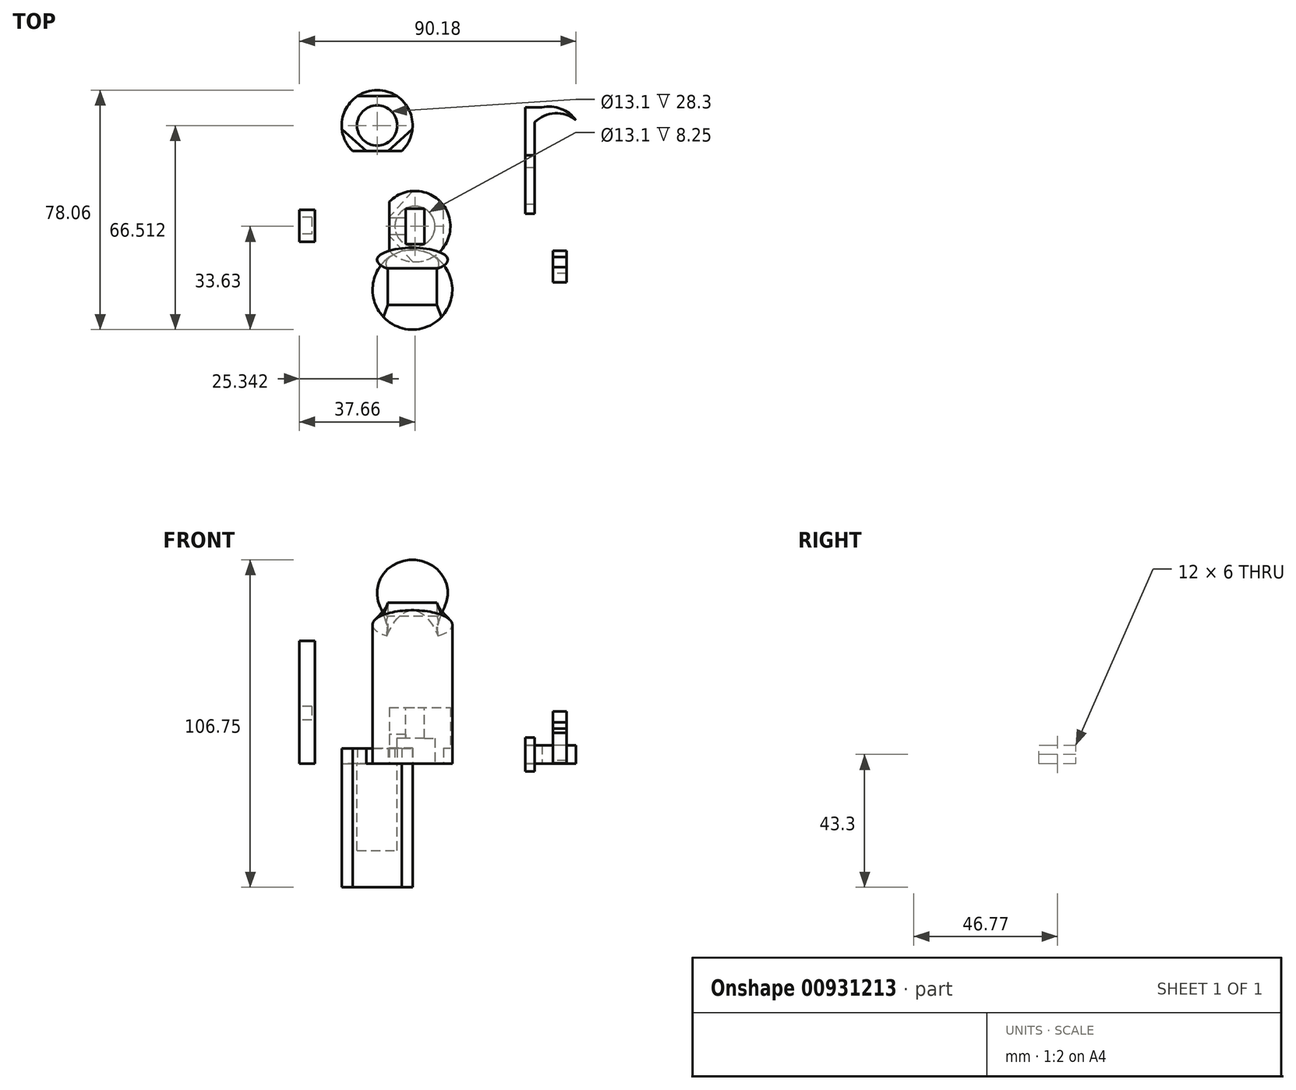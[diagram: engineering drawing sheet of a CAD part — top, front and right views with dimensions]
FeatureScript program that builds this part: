
annotation { "Feature Type Name" : "Feature", "Feature Type Description" : "" }
export const myFeature = defineFeature(function(context is Context, id is Id, definition is map)
    precondition{}
    {
        {
            var Q0;
            Q0=qCreatedBy(makeId("Top.planeOp"),FACE);
            var sketch = newSketch(context, id + "F0", { "sketchPlane" : qUnion([Q0])});
            skCircle(sketch, "E0", {"center": v(0, 0) * mm, "radius": 6.55 * mm});
            skCircle(sketch, "E1", {"center": v(0, 0) * mm, "radius": 11.55 * mm});
            skSolve(sketch);
        }
        {
            var Q0;
            Q0=makeQuery(id+"F0.imprint","IMPRINT",FACE,{"disambiguationData":[TD([[makeQuery(id+"F0.imprint","IMPRINT",EDGE,{"derivedFrom":sQuery(id+"F0.wireOp",EDGE,"E0")}),-1.0]])]});
            extrude(context, id + "F1", {"entities" : qUnion([Q0]), "depth" : (36.5 / 2) * mm, "offsetDistance" : 25 * mm});
        }
        {
            var Q0;
            Q0=makeQuery(id+"F1.opExtrude","CAP_FACE",FACE,{"disambiguationData":[OSD([sQuery(id+"F0.wireOp",EDGE,"E0"),sQuery(id+"F0.wireOp",EDGE,"E1")])],"isStart":false});
            var sketch = newSketch(context, id + "F2", { "sketchPlane" : qUnion([Q0])});
            skLineSegment(sketch, "E2", {"start": v(-3.05, 5.8) * mm, "end": v(-3.05, -5.8) * mm});
            skLineSegment(sketch, "E3", {"start": v(3.05, 5.8) * mm, "end": v(3.05, -5.8) * mm});
            skSolve(sketch);
        }
        {
            var Q0;
            {var subQ0=sQuery(id+"F2.wireOp",EDGE,"E3");Q0=makeQuery(id+"F2.imprint","IMPRINT",FACE,{"disambiguationData":[TD([[makeQuery(id+"F2.imprint","IMPRINT",EDGE,{"derivedFrom":subQ0}),1.0]])]});}
            var Q1;
            {var subQ0=sQuery(id+"F2.wireOp",EDGE,"E2");Q1=makeQuery(id+"F2.imprint","IMPRINT",FACE,{"disambiguationData":[TD([[makeQuery(id+"F2.imprint","IMPRINT",EDGE,{"derivedFrom":subQ0}),-1.0]])]});}
            extrude(context, id + "F3", {"entities" : qUnion([Q0, Q1]), "operationType" : NewBodyOperationType.ADD, "oppositeDirection" : true, "depth" : 10 * mm, "offsetDistance" : 25 * mm});
        }
        {
            var Q0;
            Q0=qCreatedBy(makeId("Top.planeOp"),FACE);
            var sketch = newSketch(context, id + "F4", { "sketchPlane" : qUnion([Q0])});
            skCircle(sketch, "E4", {"center": v(-12.32, 32.88) * mm, "radius": 6.55 * mm});
            skCircle(sketch, "E5", {"center": v(-12.32, 32.88) * mm, "radius": 11.55 * mm});
            skSolve(sketch);
        }
        {
            var Q0;
            Q0=makeQuery(id+"F4.imprint","IMPRINT",FACE,{"disambiguationData":[TD([[makeQuery(id+"F4.imprint","IMPRINT",EDGE,{"derivedFrom":sQuery(id+"F4.wireOp",EDGE,"E4")}),-1.0]])]});
            extrude(context, id + "F5", {"entities" : qUnion([Q0]), "oppositeDirection" : true, "depth" : (36.6 / 2 + 12) * mm, "offsetDistance" : 25 * mm});
        }
        {
            var Q0;
            Q0=makeQuery(id+"F5.opExtrude","CAP_FACE",FACE,{"disambiguationData":[OSD([sQuery(id+"F4.wireOp",EDGE,"E4"),sQuery(id+"F4.wireOp",EDGE,"E5")])],"isStart":false});
            var sketch = newSketch(context, id + "F6", { "sketchPlane" : qUnion([Q0])});
            skCircle(sketch, "E6", {"center": v(-12.32, -32.88) * mm, "radius": 6.55 * mm});
            skSolve(sketch);
        }
        {
            var Q0;
            Q0=makeQuery(id+"F6.imprint","IMPRINT",FACE,{"disambiguationData":[TD([[makeQuery(id+"F6.imprint","IMPRINT",EDGE,{"derivedFrom":sQuery(id+"F6.wireOp",EDGE,"E6")}),-1.0]])]});
            extrude(context, id + "F7", {"entities" : qUnion([Q0]), "operationType" : NewBodyOperationType.ADD, "oppositeDirection" : true, "depth" : 2 * mm, "offsetDistance" : 25 * mm});
        }
        {
            var Q0;
            Q0=makeQuery(id+"F7.boolean.opBoolean","MERGE",FACE,{"derivedFrom":[makeQuery(id+"F5.opExtrude","CAP_FACE",FACE,{"disambiguationData":[OSD([sQuery(id+"F4.wireOp",EDGE,"E4"),sQuery(id+"F4.wireOp",EDGE,"E5")])],"isStart":false}),makeQuery(id+"F7.opExtrude","CAP_FACE",FACE,{"disambiguationData":[OSD([sQuery(id+"F6.wireOp",EDGE,"E6")])],"isStart":true})]});
            var sketch = newSketch(context, id + "F8", { "sketchPlane" : qUnion([Q0])});
            skLineSegment(sketch, "E7", {"start": v(-20.32, -24.55) * mm, "end": v(-4.32, -24.55) * mm});
            skSolve(sketch);
        }
        {
            var Q0;
            {var subQ0=sQuery(id+"F8.wireOp",EDGE,"E7");Q0=makeQuery(id+"F8.imprint","IMPRINT",FACE,{"disambiguationData":[TD([[makeQuery(id+"F8.imprint","IMPRINT",EDGE,{"derivedFrom":subQ0}),1.0]])]});}
            extrude(context, id + "F9", {"entities" : qUnion([Q0]), "operationType" : NewBodyOperationType.REMOVE, "oppositeDirection" : true, "depth" : 40 * mm, "offsetDistance" : 25 * mm});
        }
        {
            var Q0;
            Q0=makeQuery(id+"F1.opExtrude","CAP_FACE",FACE,{"disambiguationData":[OSD([sQuery(id+"F0.wireOp",EDGE,"E0"),sQuery(id+"F0.wireOp",EDGE,"E1")])],"isStart":true});
            var sketch = newSketch(context, id + "F10", { "sketchPlane" : qUnion([Q0])});
            skLineSegment(sketch, "E8", {"start": v(-8.33, -8) * mm, "end": v(-8.33, 8) * mm});
            skSolve(sketch);
        }
        {
            var Q0;
            {var subQ0=sQuery(id+"F10.wireOp",EDGE,"E8");Q0=makeQuery(id+"F10.imprint","IMPRINT",FACE,{"disambiguationData":[TD([[makeQuery(id+"F10.imprint","IMPRINT",EDGE,{"derivedFrom":subQ0}),1.0]])]});}
            extrude(context, id + "F11", {"entities" : qUnion([Q0]), "operationType" : NewBodyOperationType.REMOVE, "oppositeDirection" : true, "depth" : 25 * mm, "offsetDistance" : 25 * mm});
        }
        {
            var Q0;
            Q0=makeQuery(id+"F11.boolean.opBoolean","COPY",FACE,{"derivedFrom":makeQuery(id+"F11.opExtrude","SWEPT_FACE",FACE,{"disambiguationData":[OSD([sQuery(id+"F10.wireOp",EDGE,"E8")])]})});
            var sketch = newSketch(context, id + "F12", { "sketchPlane" : qUnion([Q0])});
            skLineSegment(sketch, "E9.bottom", {"start": v(-2.75, 9.5) * mm, "end": v(2.75, 9.5) * mm});
            skLineSegment(sketch, "E9.top", {"start": v(-2.75, 5) * mm, "end": v(2.75, 5) * mm});
            skLineSegment(sketch, "E9.left", {"start": v(-2.75, 9.5) * mm, "end": v(-2.75, 5) * mm});
            skLineSegment(sketch, "E9.right", {"start": v(2.75, 9.5) * mm, "end": v(2.75, 5) * mm});
            skLineSegment(sketch, "E10", {"start": v(-2.75, 7.25) * mm, "end": v(-8, 7.25) * mm});
            skLineSegment(sketch, "E11", {"start": v(2.75, 7.25) * mm, "end": v(8, 7.25) * mm});
            skSolve(sketch);
        }
        {
            var Q0;
            Q0=qSketchRegion(id+"F12",true);
            extrude(context, id + "F13", {"entities" : qUnion([Q0]), "operationType" : NewBodyOperationType.REMOVE, "oppositeDirection" : true, "depth" : 10 * mm, "offsetDistance" : 25 * mm});
        }
        {
            var Q0;
            Q0=qCreatedBy(makeId("Top.planeOp"),FACE);
            var sketch = newSketch(context, id + "F14", { "sketchPlane" : qUnion([Q0])});
            skLineSegment(sketch, "E12.bottom", {"start": v(49.4, -13.29) * mm, "end": v(45, -13.29) * mm});
            skLineSegment(sketch, "E12.top", {"start": v(49.4, -9.99) * mm, "end": v(45, -9.99) * mm});
            skLineSegment(sketch, "E12.left", {"start": v(49.4, -13.29) * mm, "end": v(49.4, -9.99) * mm});
            skLineSegment(sketch, "E12.right", {"start": v(45, -13.29) * mm, "end": v(45, -9.99) * mm});
            skSolve(sketch);
        }
        {
            var Q0;
            Q0=qSketchRegion(id+"F14",true);
            extrude(context, id + "F15", {"entities" : qUnion([Q0]), "depth" : 30 * mm, "offsetDistance" : 25 * mm});
        }
        {
            var Q0;
            {var subQ0=sQuery(id+"F0.wireOp",EDGE,"E0");Q0=makeQuery(id+"F3.boolean.opBoolean","MERGE",FACE,{"derivedFrom":[makeQuery(id+"F1.opExtrude","CAP_FACE",FACE,{"disambiguationData":[OSD([subQ0,sQuery(id+"F0.wireOp",EDGE,"E1")])],"isStart":false}),makeQuery(id+"F3.opExtrude","CAP_FACE",FACE,{"disambiguationData":[OSD([subQ0,sQuery(id+"F2.wireOp",EDGE,"E2")])],"isStart":true}),makeQuery(id+"F3.opExtrude","CAP_FACE",FACE,{"disambiguationData":[OSD([subQ0,sQuery(id+"F2.wireOp",EDGE,"E3")])],"isStart":true})]});}
            var sketch = newSketch(context, id + "F16", { "sketchPlane" : qUnion([Q0])});
            skLineSegment(sketch, "E13", {"start": v(-3.05, 5.8) * mm, "end": v(3.05, 5.8) * mm});
            skLineSegment(sketch, "E14", {"start": v(3.05, -5.8) * mm, "end": v(-3.05, -5.8) * mm});
            skSolve(sketch);
        }
        {
            var Q0;
            Q0=makeQuery(id+"F16.imprint","IMPRINT",FACE,{"disambiguationData":[TD([[makeQuery(id+"F16.imprint","IMPRINT",EDGE,{"derivedFrom":sQuery(id+"F16.wireOp",EDGE,"E13")}),1.0]])]});
            var Q1;
            Q1=makeQuery(id+"F16.imprint","IMPRINT",FACE,{"disambiguationData":[TD([[makeQuery(id+"F16.imprint","IMPRINT",EDGE,{"derivedFrom":sQuery(id+"F16.wireOp",EDGE,"E14")}),1.0]])]});
            extrude(context, id + "F17", {"entities" : qUnion([Q0, Q1]), "operationType" : NewBodyOperationType.ADD, "oppositeDirection" : true, "depth" : 10 * mm, "offsetDistance" : 25 * mm});
        }
        {
            var Q0;
            Q0=qCreatedBy(makeId("Top.planeOp"),FACE);
            var sketch = newSketch(context, id + "F18", { "sketchPlane" : qUnion([Q0])});
            skLineSegment(sketch, "E15.bottom", {"start": v(-37.66, 5.43) * mm, "end": v(-32.66, 5.43) * mm});
            skLineSegment(sketch, "E15.top", {"start": v(-37.66, -4.97) * mm, "end": v(-32.66, -4.97) * mm});
            skLineSegment(sketch, "E15.left", {"start": v(-37.66, 5.43) * mm, "end": v(-37.66, -4.97) * mm});
            skLineSegment(sketch, "E15.right", {"start": v(-32.66, 5.43) * mm, "end": v(-32.66, -4.97) * mm});
            skSolve(sketch);
        }
        {
            var Q0;
            Q0=qSketchRegion(id+"F18",true);
            extrude(context, id + "F19", {"entities" : qUnion([Q0]), "depth" : 40 * mm, "offsetDistance" : 25 * mm});
        }
        {
            var Q0;
            Q0=makeQuery(id+"F19.opExtrude","SWEPT_FACE",FACE,{"disambiguationData":[OSD([sQuery(id+"F18.wireOp",EDGE,"E15.left")])]});
            var sketch = newSketch(context, id + "F20", { "sketchPlane" : qUnion([Q0])});
            skLineSegment(sketch, "E16.bottom", {"start": v(-2.98, 18.7) * mm, "end": v(2.52, 18.7) * mm});
            skLineSegment(sketch, "E16.top", {"start": v(-2.98, 14.2) * mm, "end": v(2.52, 14.2) * mm});
            skLineSegment(sketch, "E16.left", {"start": v(-2.98, 18.7) * mm, "end": v(-2.98, 14.2) * mm});
            skLineSegment(sketch, "E16.right", {"start": v(2.52, 18.7) * mm, "end": v(2.52, 14.2) * mm});
            skLineSegment(sketch, "E17", {"start": v(-2.98, 16.45) * mm, "end": v(-5.43, 16.45) * mm});
            skLineSegment(sketch, "E18", {"start": v(2.52, 16.45) * mm, "end": v(4.97, 16.45) * mm});
            skSolve(sketch);
        }
        {
            var Q0;
            Q0=qSketchRegion(id+"F20",true);
            extrude(context, id + "F21", {"entities" : qUnion([Q0]), "operationType" : NewBodyOperationType.REMOVE, "oppositeDirection" : true, "depth" : 4 * mm, "offsetDistance" : 25 * mm});
        }
        {
            var Q0;
            Q0=makeQuery(id+"F5.opExtrude","CAP_FACE",FACE,{"disambiguationData":[OSD([sQuery(id+"F4.wireOp",EDGE,"E4"),sQuery(id+"F4.wireOp",EDGE,"E5")])],"isStart":true});
            var sketch = newSketch(context, id + "F22", { "sketchPlane" : qUnion([Q0])});
            skLineSegment(sketch, "E19", {"start": v(-23.81, 31.73) * mm, "end": v(-15.83, 24.55) * mm});
            skLineSegment(sketch, "E20", {"start": v(-20.32, 24.55) * mm, "end": v(-18.31, 26.78) * mm});
            skLineSegment(sketch, "E21", {"start": v(-8.8, 24.55) * mm, "end": v(-0.83, 31.73) * mm});
            skLineSegment(sketch, "E22", {"start": v(-4.32, 24.55) * mm, "end": v(-6.33, 26.78) * mm});
            skLineSegment(sketch, "E23", {"start": v(-18.81, 42.43) * mm, "end": v(-5.82, 42.43) * mm});
            skLineSegment(sketch, "E24", {"start": v(-12.32, 44.43) * mm, "end": v(-12.32, 42.43) * mm});
            skSolve(sketch);
        }
        {
            var Q0;
            {var subQ3=sQuery(id+"F22.wireOp",EDGE,"E24");Q0=makeQuery(id+"F22.imprint","IMPRINT",FACE,{"disambiguationData":[TD([[makeQuery(id+"F22.imprint","IMPRINT",EDGE,{"derivedFrom":subQ3}),-1.0]])]});}
            var Q1;
            {var subQ3=sQuery(id+"F22.wireOp",EDGE,"E24");Q1=makeQuery(id+"F22.imprint","IMPRINT",FACE,{"disambiguationData":[TD([[makeQuery(id+"F22.imprint","IMPRINT",EDGE,{"derivedFrom":subQ3}),1.0]])]});}
            var Q2;
            {var subQ4=sQuery(id+"F22.wireOp",EDGE,"E22");Q2=makeQuery(id+"F22.imprint","IMPRINT",FACE,{"disambiguationData":[TD([[makeQuery(id+"F22.imprint","IMPRINT",EDGE,{"derivedFrom":subQ4}),-1.0]])]});}
            var Q3;
            {var subQ4=sQuery(id+"F22.wireOp",EDGE,"E22");Q3=makeQuery(id+"F22.imprint","IMPRINT",FACE,{"disambiguationData":[TD([[makeQuery(id+"F22.imprint","IMPRINT",EDGE,{"derivedFrom":subQ4}),1.0]])]});}
            var Q4;
            {var subQ4=sQuery(id+"F22.wireOp",EDGE,"E20");Q4=makeQuery(id+"F22.imprint","IMPRINT",FACE,{"disambiguationData":[TD([[makeQuery(id+"F22.imprint","IMPRINT",EDGE,{"derivedFrom":subQ4}),-1.0]])]});}
            var Q5;
            {var subQ4=sQuery(id+"F22.wireOp",EDGE,"E20");Q5=makeQuery(id+"F22.imprint","IMPRINT",FACE,{"disambiguationData":[TD([[makeQuery(id+"F22.imprint","IMPRINT",EDGE,{"derivedFrom":subQ4}),1.0]])]});}
            extrude(context, id + "F23", {"entities" : qUnion([Q0, Q1, Q2, Q3, Q4, Q5]), "operationType" : NewBodyOperationType.ADD, "depth" : 5 * mm, "offsetDistance" : 25 * mm});
        }
        {
            var Q0;
            Q0=makeQuery(id+"F1.opExtrude","CAP_FACE",FACE,{"disambiguationData":[OSD([sQuery(id+"F0.wireOp",EDGE,"E0"),sQuery(id+"F0.wireOp",EDGE,"E1")])],"isStart":true});
            var sketch = newSketch(context, id + "F24", { "sketchPlane" : qUnion([Q0])});
            skLineSegment(sketch, "E25", {"start": v(-0.71, 11.53) * mm, "end": v(-8.33, 3.07) * mm});
            skLineSegment(sketch, "E26", {"start": v(-0.71, -11.53) * mm, "end": v(-8.33, -3.07) * mm});
            skLineSegment(sketch, "E27", {"start": v(9.25, 6.92) * mm, "end": v(9.25, -6.92) * mm});
            skLineSegment(sketch, "E28", {"start": v(11.55, 0) * mm, "end": v(9.25, 0) * mm});
            skLineSegment(sketch, "E29", {"start": v(-8.33, -8) * mm, "end": v(-5.88, -5.8) * mm});
            skLineSegment(sketch, "E30", {"start": v(-8.33, 8) * mm, "end": v(-5.88, 5.8) * mm});
            skSolve(sketch);
        }
        {
            var Q0;
            {var subQ4=sQuery(id+"F24.wireOp",EDGE,"E29");Q0=makeQuery(id+"F24.imprint","IMPRINT",FACE,{"disambiguationData":[TD([[makeQuery(id+"F24.imprint","IMPRINT",EDGE,{"derivedFrom":subQ4}),1.0]])]});}
            var Q1;
            {var subQ5=sQuery(id+"F24.wireOp",EDGE,"E29");Q1=makeQuery(id+"F24.imprint","IMPRINT",FACE,{"disambiguationData":[TD([[makeQuery(id+"F24.imprint","IMPRINT",EDGE,{"derivedFrom":subQ5}),-1.0]])]});}
            var Q2;
            {var subQ5=sQuery(id+"F24.wireOp",EDGE,"E30");Q2=makeQuery(id+"F24.imprint","IMPRINT",FACE,{"disambiguationData":[TD([[makeQuery(id+"F24.imprint","IMPRINT",EDGE,{"derivedFrom":subQ5}),1.0]])]});}
            var Q3;
            {var subQ4=sQuery(id+"F24.wireOp",EDGE,"E30");Q3=makeQuery(id+"F24.imprint","IMPRINT",FACE,{"disambiguationData":[TD([[makeQuery(id+"F24.imprint","IMPRINT",EDGE,{"derivedFrom":subQ4}),-1.0]])]});}
            var Q4;
            {var subQ3=sQuery(id+"F24.wireOp",EDGE,"E28");Q4=makeQuery(id+"F24.imprint","IMPRINT",FACE,{"disambiguationData":[TD([[makeQuery(id+"F24.imprint","IMPRINT",EDGE,{"derivedFrom":subQ3}),1.0]])]});}
            var Q5;
            {var subQ3=sQuery(id+"F24.wireOp",EDGE,"E28");Q5=makeQuery(id+"F24.imprint","IMPRINT",FACE,{"disambiguationData":[TD([[makeQuery(id+"F24.imprint","IMPRINT",EDGE,{"derivedFrom":subQ3}),-1.0]])]});}
            extrude(context, id + "F25", {"entities" : qUnion([Q0, Q1, Q2, Q3, Q4, Q5]), "operationType" : NewBodyOperationType.REMOVE, "oppositeDirection" : true, "depth" : 5.1 * mm, "offsetDistance" : 25 * mm});
        }
        {
            var Q0;
            Q0=makeQuery(id+"F15.opExtrude","CAP_EDGE",EDGE,{"disambiguationData":[OSD([sQuery(id+"F14.wireOp",EDGE,"E12.top")])],"isStart":true});
            chamfer(context, id + "F26", {"entities" : qUnion([Q0]), "chamferType" : ChamferType.TWO_OFFSETS, "width1" : 3.7 * mm, "oppositeDirection" : false, "width2" : 1 * mm});
        }
        {
            var Q0;
            Q0=makeQuery(id+"F15.opExtrude","CAP_FACE",FACE,{"disambiguationData":[OSD([sQuery(id+"F14.wireOp",EDGE,"E12.bottom"),sQuery(id+"F14.wireOp",EDGE,"E12.top"),sQuery(id+"F14.wireOp",EDGE,"E12.left"),sQuery(id+"F14.wireOp",EDGE,"E12.right")])],"isStart":false});
            var sketch = newSketch(context, id + "F27", { "sketchPlane" : qUnion([Q0])});
            skLineSegment(sketch, "E31.bottom", {"start": v(39.7, -13.29) * mm, "end": v(54.7, -13.29) * mm});
            skLineSegment(sketch, "E31.top", {"start": v(39.7, -8.29) * mm, "end": v(54.7, -8.29) * mm});
            skLineSegment(sketch, "E31.left", {"start": v(39.7, -13.29) * mm, "end": v(39.7, -8.29) * mm});
            skLineSegment(sketch, "E31.right", {"start": v(54.7, -13.29) * mm, "end": v(54.7, -8.29) * mm});
            skLineSegment(sketch, "E32", {"start": v(39.7, -9.99) * mm, "end": v(45, -9.99) * mm});
            skLineSegment(sketch, "E33", {"start": v(49.4, -9.99) * mm, "end": v(54.7, -9.99) * mm});
            skSolve(sketch);
        }
        {
            var Q0;
            {var subQ4=sQuery(id+"F27.wireOp",EDGE,"E32");Q0=makeQuery(id+"F27.imprint","IMPRINT",FACE,{"disambiguationData":[TD([[makeQuery(id+"F27.imprint","IMPRINT",EDGE,{"derivedFrom":subQ4}),-1.0]])]});}
            cPlane(context, id + "F28", {"entities" : qUnion([Q0]), "cplaneType" : CPlaneType.OFFSET, "offset" : 20 * mm, "oppositeDirection" : true, "width" : 150 * mm, "height" : 150 * mm});
        }
        {
            var Q0;
            Q0=qCreatedBy(id+"F28.planeOp",FACE);
            var sketch = newSketch(context, id + "F29", { "sketchPlane" : qUnion([Q0])});
            skLineSegment(sketch, "E34.0.0", {"start": v(45, -13.29) * mm, "end": v(45, -10.99) * mm});
            skLineSegment(sketch, "E34.0.1", {"start": v(45, -10.99) * mm, "end": v(49.4, -10.99) * mm});
            skLineSegment(sketch, "E34.0.2", {"start": v(49.4, -10.99) * mm, "end": v(49.4, -13.29) * mm});
            skLineSegment(sketch, "E34.0.3", {"start": v(49.4, -13.29) * mm, "end": v(45, -13.29) * mm});
            skLineSegment(sketch, "E35.bottom", {"start": v(42.2, -13.29) * mm, "end": v(52.2, -13.29) * mm});
            skLineSegment(sketch, "E35.top", {"start": v(42.2, -10.09) * mm, "end": v(52.2, -10.09) * mm});
            skLineSegment(sketch, "E35.left", {"start": v(42.2, -13.29) * mm, "end": v(42.2, -10.09) * mm});
            skLineSegment(sketch, "E35.right", {"start": v(52.2, -13.29) * mm, "end": v(52.2, -10.09) * mm});
            skLineSegment(sketch, "E36", {"start": v(45, -10.99) * mm, "end": v(42.2, -10.99) * mm});
            skLineSegment(sketch, "E37", {"start": v(49.4, -10.99) * mm, "end": v(52.2, -10.99) * mm});
            skSolve(sketch);
        }
        {
            var Q0;
            Q0=qCreatedBy(makeId("Top.planeOp"),FACE);
            var sketch = newSketch(context, id + "F30", { "sketchPlane" : qUnion([Q0])});
            skCircle(sketch, "E38", {"center": v(-0.83, -20.63) * mm, "radius": 13 * mm});
            skSolve(sketch);
        }
        {
            var Q0;
            Q0=makeQuery(id+"F30.imprint","IMPRINT",FACE,{"disambiguationData":[TD([[makeQuery(id+"F30.imprint","IMPRINT",EDGE,{"derivedFrom":sQuery(id+"F30.wireOp",EDGE,"E38")}),1.0]])]});
            extrude(context, id + "F31", {"entities" : qUnion([Q0]), "depth" : 50 * mm, "offsetDistance" : 25 * mm});
        }
        {
            var Q0;
            Q0=makeQuery(id+"F31.opExtrude","CAP_FACE",FACE,{"disambiguationData":[OSD([sQuery(id+"F30.wireOp",EDGE,"E38")])],"isStart":false});
            var sketch = newSketch(context, id + "F32", { "sketchPlane" : qUnion([Q0])});
            skLineSegment(sketch, "E39.bottom", {"start": v(-5.1, -22.85) * mm, "end": v(-0.43, -22.85) * mm});
            skLineSegment(sketch, "E39.top", {"start": v(-5.1, -18.54) * mm, "end": v(-0.43, -18.54) * mm});
            skLineSegment(sketch, "E39.left", {"start": v(-5.1, -22.85) * mm, "end": v(-5.1, -18.54) * mm});
            skLineSegment(sketch, "E39.right", {"start": v(-0.43, -22.85) * mm, "end": v(-0.43, -18.54) * mm});
            skSolve(sketch);
        }
        {
            var Q0;
            Q0 = qSketchRegion(id + "F32", true);
            extrude(context, id + "F33", {"entities" : qUnion([Q0]), "operationType" : NewBodyOperationType.REMOVE, "oppositeDirection" : true, "depth" : .1 * mm, "offsetDistance" : 25 * mm});
        }
        {
            var Q0;
            Q0=makeQuery(id+"F33.boolean.opBoolean","COPY",FACE,{"derivedFrom":makeQuery(id+"F33.opExtrude","SWEPT_FACE",FACE,{"disambiguationData":[OSD([sQuery(id+"F32.wireOp",EDGE,"E39.left")])]})});
            cPlane(context, id + "F34", {"entities" : qUnion([Q0]), "cplaneType" : CPlaneType.OFFSET, "offset" : 3 * mm, "width" : 150 * mm, "height" : 150 * mm});
        }
        {
            var Q0;
            Q0=qCreatedBy(id+"F34.planeOp",FACE);
            var sketch = newSketch(context, id + "F35", { "sketchPlane" : qUnion([Q0])});
            skLineSegment(sketch, "E40.0", {"start": v(-33.63, 50) * mm, "end": v(-7.63, 50) * mm});
            skLineSegment(sketch, "E41", {"start": v(-33.63, 0) * mm, "end": v(-33.63, 50) * mm});
            skLineSegment(sketch, "E42", {"start": v(-7.63, 50) * mm, "end": v(-7.63, 0) * mm});
            skLineSegment(sketch, "E43", {"start": v(-33.63, 50) * mm, "end": v(-10.67, 41.64) * mm});
            skLineSegment(sketch, "E44", {"start": v(-10.67, 41.64) * mm, "end": v(-7.63, 50) * mm});
            skSolve(sketch);
        }
        {
            var Q0;
            Q0 = qSketchRegion(id + "F35", true);
            extrude(context, id + "F36", {"entities" : qUnion([Q0]), "operationType" : NewBodyOperationType.REMOVE, "oppositeDirection" : true, "depth" : 30 * mm, "offsetDistance" : 25 * mm, "symmetric" : true});
        }
        {
            var Q0;
            Q0=makeQuery(id+"F36.boolean.opBoolean","COPY",FACE,{"derivedFrom":makeQuery(id+"F36.opExtrude","SWEPT_FACE",FACE,{"disambiguationData":[OSD([sQuery(id+"F35.wireOp",EDGE,"E44")])]})});
            cPlane(context, id + "F37", {"entities" : qUnion([Q0]), "cplaneType" : CPlaneType.OFFSET, "offset" : 5 * mm, "width" : 150 * mm, "height" : 150 * mm});
        }
        {
            var Q0;
            Q0=qCreatedBy(id+"F34.planeOp",FACE);
            var sketch = newSketch(context, id + "F38", { "sketchPlane" : qUnion([Q0])});
            skPoint(sketch, "E45.0", {"position": v(-10.67, 41.64) * mm});
            skLineSegment(sketch, "E46", {"start": v(-10.67, 41.64) * mm, "end": v(-10.67, 46.64) * mm});
            skSolve(sketch);
        }
        {
            var Q0;
            Q0=qCreatedBy(id+"F37.planeOp",FACE);
            var sketch = newSketch(context, id + "F39", { "sketchPlane" : qUnion([Q0])});
            skLineSegment(sketch, "E47", {"start": v(7.17, 40.18) * mm, "end": v(-8.83, 40.18) * mm});
            skArc(sketch, "E48", {"start": v(7.17, 40.18) * mm, "mid": v(-0.83, 60.06) * mm, "end": v(-8.83, 40.18) * mm});
            skLineSegment(sketch, "E49", {"start": v(12.17, 11.57) * mm, "end": v(12.17, -14.59) * mm});
            skLineSegment(sketch, "E50", {"start": v(-13.83, -14.59) * mm, "end": v(-13.83, 11.57) * mm});
            skPoint(sketch, "E51.0.start.orphan", {"position": v(7.53, 35.48) * mm});
            skPoint(sketch, "E52.trimOffspring.end.orphan", {"position": v(-9.18, 35.48) * mm});
            skSolve(sketch);
        }
        {
            var Q1;
            Q1=makeQuery(id+"F36.boolean.opBoolean","COPY",FACE,{"derivedFrom":makeQuery(id+"F36.opExtrude","SWEPT_FACE",FACE,{"disambiguationData":[OSD([sQuery(id+"F35.wireOp",EDGE,"E44")])]})});
            var Q2;
            Q2=makeQuery(id+"F39.imprint","IMPRINT",FACE,{"disambiguationData":[TD([[makeQuery(id+"F39.imprint","IMPRINT",EDGE,{"derivedFrom":sQuery(id+"F39.wireOp",EDGE,"E47")}),-1.0]])]});
            loft(context, id + "F40", {"operationType" : NewBodyOperationType.ADD, "sheetProfilesArray" : [{ "sheetProfileEntities" : qUnion([Q1]) }, { "sheetProfileEntities" : qUnion([Q2]) }]});
        }
        {
            var Q0;
            Q0=makeQuery(id+"F36.boolean.opBoolean","COPY",FACE,{"derivedFrom":makeQuery(id+"F36.opExtrude","SWEPT_FACE",FACE,{"disambiguationData":[OSD([sQuery(id+"F35.wireOp",EDGE,"E43")])]})});
            cPlane(context, id + "F41", {"entities" : qUnion([Q0]), "cplaneType" : CPlaneType.OFFSET, "offset" : 5 * mm, "width" : 150 * mm, "height" : 150 * mm});
        }
        {
            var Q0;
            Q0=qCreatedBy(id+"F41.planeOp",FACE);
            var sketch = newSketch(context, id + "F42", { "sketchPlane" : qUnion([Q0])});
            skLineSegment(sketch, "E53.bottom", {"start": v(-8.83, -41.98) * mm, "end": v(7.17, -41.98) * mm});
            skLineSegment(sketch, "E53.top", {"start": v(-8.83, -25.98) * mm, "end": v(7.17, -25.98) * mm});
            skLineSegment(sketch, "E53.left", {"start": v(-8.83, -41.98) * mm, "end": v(-8.83, -25.98) * mm});
            skLineSegment(sketch, "E53.right", {"start": v(7.17, -41.98) * mm, "end": v(7.17, -25.98) * mm});
            skLineSegment(sketch, "E54", {"start": v(-13.83, -40.75) * mm, "end": v(-13.83, -14.59) * mm});
            skLineSegment(sketch, "E55", {"start": v(12.17, -14.59) * mm, "end": v(12.17, -40.75) * mm});
            skSolve(sketch);
        }
        {
            var Q1;
            Q1=makeQuery(id+"F36.boolean.opBoolean","COPY",FACE,{"derivedFrom":makeQuery(id+"F36.opExtrude","SWEPT_FACE",FACE,{"disambiguationData":[OSD([sQuery(id+"F35.wireOp",EDGE,"E43")])]})});
            var Q2;
            Q2=makeQuery(id+"F42.imprint","IMPRINT",FACE,{"disambiguationData":[TD([[makeQuery(id+"F42.imprint","IMPRINT",EDGE,{"derivedFrom":sQuery(id+"F42.wireOp",EDGE,"E53.bottom")}),1.0]])]});
            loft(context, id + "F43", {"operationType" : NewBodyOperationType.ADD, "sheetProfilesArray" : [{ "sheetProfileEntities" : qUnion([Q1]) }, { "sheetProfileEntities" : qUnion([Q2]) }]});
        }
        {
            var Q0;
            Q0=makeQuery(id+"F15.opExtrude","SWEPT_FACE",FACE,{"disambiguationData":[OSD([sQuery(id+"F14.wireOp",EDGE,"E12.right")])]});
            var sketch = newSketch(context, id + "F44", { "sketchPlane" : qUnion([Q0])});
            skLineSegment(sketch, "E56.0", {"start": v(10.99, 10) * mm, "end": v(13.29, 10) * mm});
            skLineSegment(sketch, "E57", {"start": v(13.29, 10) * mm, "end": v(18.29, 13.5) * mm});
            skLineSegment(sketch, "E58", {"start": v(18.29, 13.5) * mm, "end": v(13.29, 13.5) * mm});
            skSolve(sketch);
        }
        {
            var Q0;
            {var subQ0=sQuery(id+"F44.wireOp",EDGE,"E57");Q0=makeQuery(id+"F44.imprint","IMPRINT",FACE,{"disambiguationData":[TD([[makeQuery(id+"F44.imprint","IMPRINT",EDGE,{"derivedFrom":subQ0}),1.0]])]});}
            var Q1;
            Q1=makeQuery(id+"F15.opExtrude","SWEPT_FACE",FACE,{"disambiguationData":[OSD([sQuery(id+"F14.wireOp",EDGE,"E12.left")])]});
            extrude(context, id + "F45", {"entities" : qUnion([Q0]), "operationType" : NewBodyOperationType.ADD, "endBound" : BoundingType.UP_TO_SURFACE, "oppositeDirection" : true, "depth" : 25 * mm, "endBoundEntityFace" : qUnion([Q1]), "offsetDistance" : 25 * mm});
        }
        {
            var Q0;
            {var subQ0=sQuery(id+"F14.wireOp",EDGE,"E12.right");Q0=makeQuery(id+"F45.boolean.opBoolean","MERGE",FACE,{"derivedFrom":[makeQuery(id+"F15.opExtrude","SWEPT_FACE",FACE,{"disambiguationData":[OSD([subQ0])]}),makeQuery(id+"F45.opExtrude","CAP_FACE",FACE,{"disambiguationData":[OSD([sQuery(id+"F14.wireOp",EDGE,"E12.bottom"),subQ0,sQuery(id+"F44.wireOp",EDGE,"E57"),sQuery(id+"F44.wireOp",EDGE,"E58")])],"isStart":true})]});}
            var sketch = newSketch(context, id + "F46", { "sketchPlane" : qUnion([Q0])});
            skLineSegment(sketch, "E59.0", {"start": v(10.99, 10) * mm, "end": v(13.29, 10) * mm});
            skLineSegment(sketch, "E60.bottom", {"start": v(15.29, 10) * mm, "end": v(7.99, 10) * mm});
            skLineSegment(sketch, "E60.top", {"start": v(15.29, 13.5) * mm, "end": v(7.99, 13.5) * mm});
            skLineSegment(sketch, "E60.left", {"start": v(15.29, 10) * mm, "end": v(15.29, 13.5) * mm});
            skLineSegment(sketch, "E60.right", {"start": v(7.99, 10) * mm, "end": v(7.99, 13.5) * mm});
            skSolve(sketch);
        }
        {
            var Q0;
            Q0 = qSketchRegion(id + "F46", true);
            var Q1;
            Q1=makeQuery(id+"F45.boolean.opBoolean","MERGE",FACE,{"derivedFrom":[makeQuery(id+"F15.opExtrude","SWEPT_FACE",FACE,{"disambiguationData":[OSD([sQuery(id+"F14.wireOp",EDGE,"E12.left")])]}),makeQuery(id+"F45.opExtrude","CAP_FACE",FACE,{"disambiguationData":[OSD([sQuery(id+"F14.wireOp",EDGE,"E12.bottom"),sQuery(id+"F14.wireOp",EDGE,"E12.right"),sQuery(id+"F44.wireOp",EDGE,"E57"),sQuery(id+"F44.wireOp",EDGE,"E58")])],"isStart":false})]});
            extrude(context, id + "F47", {"entities" : qUnion([Q0]), "operationType" : NewBodyOperationType.ADD, "endBound" : BoundingType.UP_TO_SURFACE, "oppositeDirection" : true, "depth" : 25 * mm, "endBoundEntityFace" : qUnion([Q1]), "offsetDistance" : 25 * mm});
        }
        {
            var Q0;
            Q0=makeQuery(id+"F15.opExtrude","CAP_FACE",FACE,{"disambiguationData":[OSD([sQuery(id+"F14.wireOp",EDGE,"E12.bottom"),sQuery(id+"F14.wireOp",EDGE,"E12.top"),sQuery(id+"F14.wireOp",EDGE,"E12.left"),sQuery(id+"F14.wireOp",EDGE,"E12.right")])],"isStart":false});
            extrude(context, id + "F48", {"entities" : qUnion([Q0]), "operationType" : NewBodyOperationType.REMOVE, "oppositeDirection" : true, "depth" : 13 * mm, "offsetDistance" : 25 * mm});
        }
        {
            var Q0;
            Q0=qCreatedBy(makeId("Top.planeOp"),FACE);
            var sketch = newSketch(context, id + "F49", { "sketchPlane" : qUnion([Q0])});
            skArc(sketch, "E61", {"start": v(52.52, 34.58) * mm, "mid": v(45.64, 36.88) * mm, "end": v(39.02, 33.92) * mm});
            skArc(sketch, "E62", {"start": v(52.52, 34.58) * mm, "mid": v(44.57, 39) * mm, "end": v(36.02, 35.9) * mm});
            skLineSegment(sketch, "E63", {"start": v(36.02, 35.9) * mm, "end": v(36.02, 19.14) * mm});
            skLineSegment(sketch, "E64", {"start": v(39.02, 33.92) * mm, "end": v(39.02, 19.14) * mm});
            skLineSegment(sketch, "E65", {"start": v(39.02, 19.14) * mm, "end": v(36.02, 19.14) * mm});
            skSolve(sketch);
        }
        {
            var Q0;
            Q0 = qSketchRegion(id + "F49", true);
            extrude(context, id + "F50", {"entities" : qUnion([Q0]), "depth" : 6 * mm, "offsetDistance" : 25 * mm});
        }
        {
            var Q0;
            Q0=makeQuery(id+"F50.opExtrude","SWEPT_FACE",FACE,{"disambiguationData":[OSD([sQuery(id+"F49.wireOp",EDGE,"E63")])]});
            var sketch = newSketch(context, id + "F51", { "sketchPlane" : qUnion([Q0])});
            skLineSegment(sketch, "E66.bottom", {"start": v(-23.14, 6) * mm, "end": v(-7.14, 6) * mm});
            skLineSegment(sketch, "E66.top", {"start": v(-23.14, 8.5) * mm, "end": v(-7.14, 8.5) * mm});
            skLineSegment(sketch, "E66.left", {"start": v(-23.14, 6) * mm, "end": v(-23.14, 8.5) * mm});
            skLineSegment(sketch, "E66.right", {"start": v(-7.14, 6) * mm, "end": v(-7.14, 8.5) * mm});
            skLineSegment(sketch, "E67.bottom", {"start": v(-23.14, 0) * mm, "end": v(-7.14, 0) * mm});
            skLineSegment(sketch, "E67.top", {"start": v(-23.14, -2.5) * mm, "end": v(-7.14, -2.5) * mm});
            skLineSegment(sketch, "E67.left", {"start": v(-23.14, 0) * mm, "end": v(-23.14, -2.5) * mm});
            skLineSegment(sketch, "E67.right", {"start": v(-7.14, 0) * mm, "end": v(-7.14, -2.5) * mm});
            skLineSegment(sketch, "E68.bottom", {"start": v(-7.14, 8.5) * mm, "end": v(-4.14, 8.5) * mm});
            skLineSegment(sketch, "E68.top", {"start": v(-7.14, -2.5) * mm, "end": v(-4.14, -2.5) * mm});
            skLineSegment(sketch, "E68.left", {"start": v(-7.14, 8.5) * mm, "end": v(-7.14, -2.5) * mm});
            skLineSegment(sketch, "E68.right", {"start": v(-4.14, 8.5) * mm, "end": v(-4.14, -2.5) * mm});
            skSolve(sketch);
        }
        {
            var Q0;
            {var subQ1=sQuery(id+"F51.wireOp",EDGE,"E67.top");Q0=makeQuery(id+"F51.imprint","IMPRINT",FACE,{"disambiguationData":[TD([[makeQuery(id+"F51.imprint","IMPRINT",EDGE,{"derivedFrom":subQ1}),1.0]])]});}
            var Q1;
            {var subQ3=sQuery(id+"F51.wireOp",EDGE,"E68.bottom");Q1=makeQuery(id+"F51.imprint","IMPRINT",FACE,{"disambiguationData":[TD([[makeQuery(id+"F51.imprint","IMPRINT",EDGE,{"derivedFrom":subQ3}),-1.0]])]});}
            var Q2;
            {var subQ1=sQuery(id+"F51.wireOp",EDGE,"E66.top");Q2=makeQuery(id+"F51.imprint","IMPRINT",FACE,{"disambiguationData":[TD([[makeQuery(id+"F51.imprint","IMPRINT",EDGE,{"derivedFrom":subQ1}),-1.0]])]});}
            var Q3;
            Q3=makeQuery(id+"F50.opExtrude","SWEPT_FACE",FACE,{"disambiguationData":[OSD([sQuery(id+"F49.wireOp",EDGE,"E64")])]});
            extrude(context, id + "F52", {"entities" : qUnion([Q0, Q1, Q2]), "operationType" : NewBodyOperationType.ADD, "endBound" : BoundingType.UP_TO_SURFACE, "oppositeDirection" : true, "depth" : 25 * mm, "endBoundEntityFace" : qUnion([Q3]), "offsetDistance" : 25 * mm});
        }
        {
            var Q0;
            Q0=makeQuery(id+"F50.opExtrude","CAP_FACE",FACE,{"disambiguationData":[OSD([sQuery(id+"F49.wireOp",EDGE,"E61"),sQuery(id+"F49.wireOp",EDGE,"E62"),sQuery(id+"F49.wireOp",EDGE,"E63"),sQuery(id+"F49.wireOp",EDGE,"E64"),sQuery(id+"F49.wireOp",EDGE,"E65")])],"isStart":true});
            var sketch = newSketch(context, id + "F53", { "sketchPlane" : qUnion([Q0])});
            skLineSegment(sketch, "E69.bottom", {"start": v(36.02, -35.9) * mm, "end": v(41.4, -35.9) * mm});
            skLineSegment(sketch, "E69.top", {"start": v(36.02, -38.8) * mm, "end": v(41.4, -38.8) * mm});
            skLineSegment(sketch, "E69.left", {"start": v(36.02, -35.9) * mm, "end": v(36.02, -38.8) * mm});
            skLineSegment(sketch, "E69.right", {"start": v(41.4, -35.9) * mm, "end": v(41.4, -38.8) * mm});
            skSolve(sketch);
        }
        {
            var Q0;
            Q0 = qSketchRegion(id + "F53", true);
            var Q1;
            Q1=makeQuery(id+"F50.opExtrude","CAP_FACE",FACE,{"disambiguationData":[OSD([sQuery(id+"F49.wireOp",EDGE,"E61"),sQuery(id+"F49.wireOp",EDGE,"E62"),sQuery(id+"F49.wireOp",EDGE,"E63"),sQuery(id+"F49.wireOp",EDGE,"E64"),sQuery(id+"F49.wireOp",EDGE,"E65")])],"isStart":false});
            extrude(context, id + "F54", {"entities" : qUnion([Q0]), "operationType" : NewBodyOperationType.ADD, "endBound" : BoundingType.UP_TO_SURFACE, "oppositeDirection" : true, "depth" : 25 * mm, "endBoundEntityFace" : qUnion([Q1]), "offsetDistance" : 25 * mm});
        }
        {
            var Q0;
            Q0=makeQuery(id+"F7.boolean.opBoolean","MERGE",FACE,{"derivedFrom":[makeQuery(id+"F5.opExtrude","CAP_FACE",FACE,{"disambiguationData":[OSD([sQuery(id+"F4.wireOp",EDGE,"E4"),sQuery(id+"F4.wireOp",EDGE,"E5")])],"isStart":false}),makeQuery(id+"F7.opExtrude","CAP_FACE",FACE,{"disambiguationData":[OSD([sQuery(id+"F6.wireOp",EDGE,"E6")])],"isStart":true})]});
            extrude(context, id + "F55", {"entities" : qUnion([Q0]), "operationType" : NewBodyOperationType.ADD, "depth" : 10 * mm, "offsetDistance" : 25 * mm});
        }
    });
